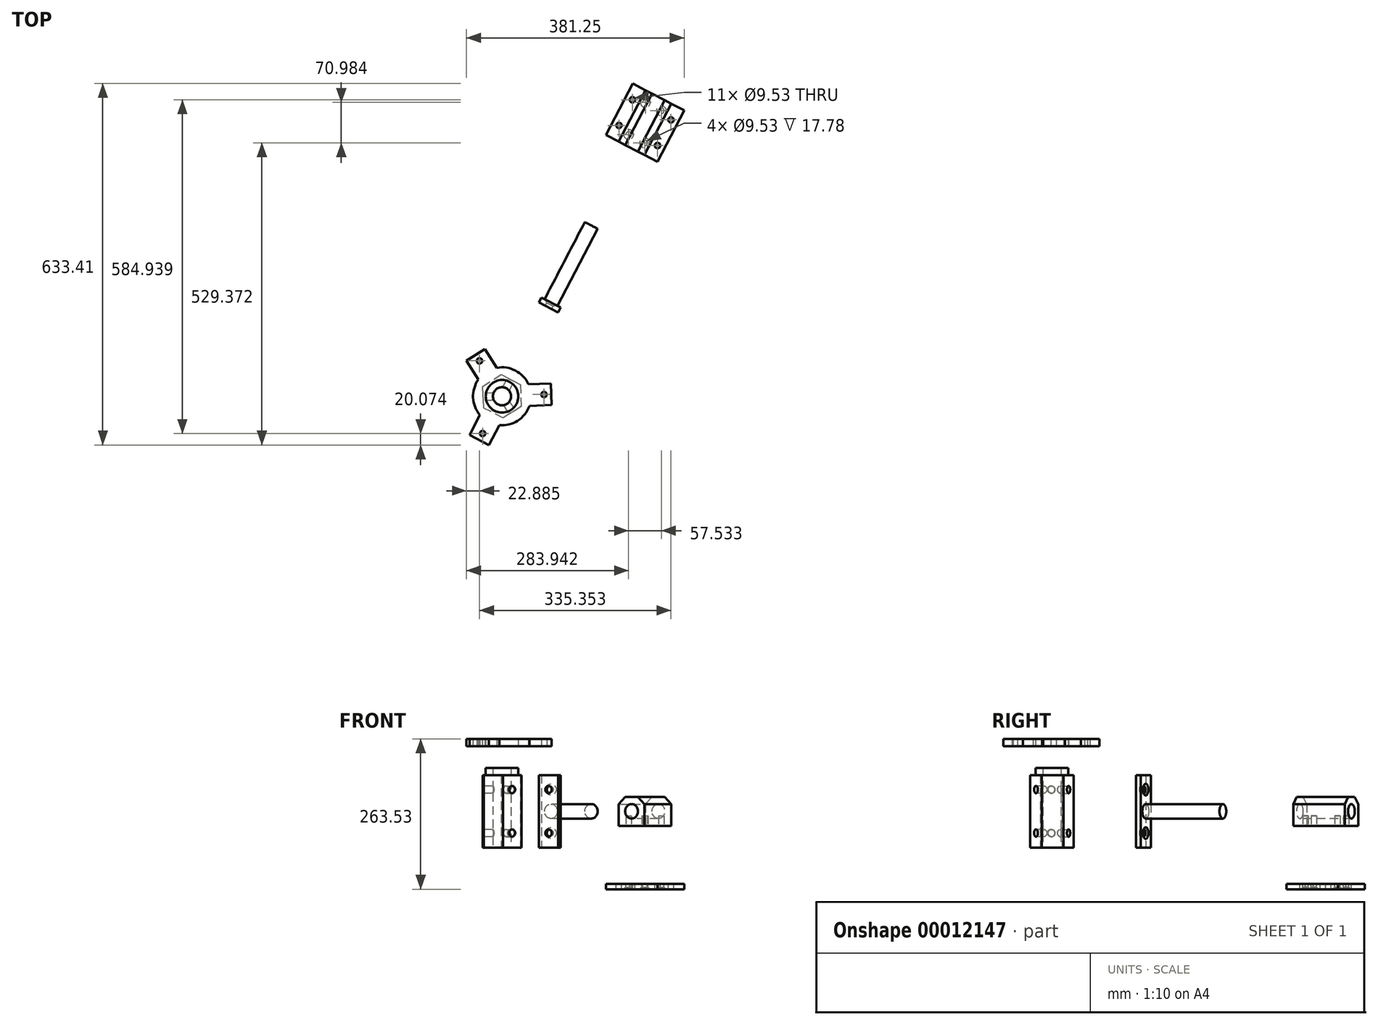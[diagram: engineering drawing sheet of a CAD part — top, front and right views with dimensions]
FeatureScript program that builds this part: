
annotation { "Feature Type Name" : "Feature", "Feature Type Description" : "" }
export const myFeature = defineFeature(function(context is Context, id is Id, definition is map)
    precondition{}
    {
        {
            var Q0;
            Q0=qCreatedBy(makeId("Top.planeOp"),FACE);
            var sketch = newSketch(context, id + "F0", { "sketchPlane" : qUnion([Q0])});
            skCircle(sketch, "E0.cCircle", {"center": v(0, 0) * mm, "radius": 33 * mm, "construction": true});
            skLineSegment(sketch, "E0.0", {"start": v(-1.62, 38.07) * mm, "end": v(32.16, 20.43) * mm});
            skLineSegment(sketch, "E0.1", {"start": v(32.16, 20.43) * mm, "end": v(33.77, -17.63) * mm});
            skLineSegment(sketch, "E0.2", {"start": v(33.77, -17.63) * mm, "end": v(1.62, -38.07) * mm});
            skLineSegment(sketch, "E0.3", {"start": v(1.62, -38.07) * mm, "end": v(-32.16, -20.43) * mm});
            skLineSegment(sketch, "E0.4", {"start": v(-32.16, -20.43) * mm, "end": v(-33.77, 17.63) * mm});
            skLineSegment(sketch, "E0.5", {"start": v(-33.77, 17.63) * mm, "end": v(-1.62, 38.07) * mm});
            skPoint(sketch, "E0.0.midPoint", {"position": v(15.27, 29.25) * mm});
            skCircle(sketch, "E1", {"center": v(0, 0) * mm, "radius": 15.88 * mm});
            skSolve(sketch);
        }
        {
            var Q0;
            Q0=makeQuery(id+"F0.imprint","IMPRINT",FACE,{"disambiguationData":[TD([[makeQuery(id+"F0.imprint","IMPRINT",EDGE,{"derivedFrom":sQuery(id+"F0.wireOp",EDGE,"E0.0")}),-1.0]])]});
            extrude(context, id + "F1", {"entities" : qUnion([Q0]), "depth" : 127 * mm});
        }
        {
            var Q0;
            Q0=makeQuery(id+"F1.opExtrude","SWEPT_FACE",FACE,{"disambiguationData":[OSD([sQuery(id+"F0.wireOp",EDGE,"E0.2")])]});
            var sketch = newSketch(context, id + "F2", { "sketchPlane" : qUnion([Q0]), "disableImprinting" : false});
            skLineSegment(sketch, "E2", {"start": v(0, 127) * mm, "end": v(0, 0) * mm, "construction": true});
            skLineSegment(sketch, "E3", {"start": v(-19.05, 63.5) * mm, "end": v(19.05, 63.5) * mm, "construction": true});
            skLineSegment(sketch, "E4.0", {"start": v(-19.05, 101.6) * mm, "end": v(19.05, 101.6) * mm, "construction": true});
            skLineSegment(sketch, "E5.0", {"start": v(-19.05, 25.4) * mm, "end": v(19.05, 25.4) * mm, "construction": true});
            skCircle(sketch, "E6", {"center": v(0, 101.6) * mm, "radius": 6.35 * mm});
            skCircle(sketch, "E7", {"center": v(0, 25.4) * mm, "radius": 6.35 * mm});
            skSolve(sketch);
        }
        {
            var Q0;
            Q0=makeQuery(id+"F1.opExtrude","SWEPT_FACE",FACE,{"disambiguationData":[OSD([sQuery(id+"F0.wireOp",EDGE,"E0.0")])]});
            var sketch = newSketch(context, id + "F3", { "sketchPlane" : qUnion([Q0]), "disableImprinting" : false});
            skLineSegment(sketch, "E8", {"start": v(0, 127) * mm, "end": v(0, 0) * mm, "construction": true});
            skLineSegment(sketch, "E9", {"start": v(19.05, 63.5) * mm, "end": v(-19.05, 63.5) * mm, "construction": true});
            skLineSegment(sketch, "E10.0", {"start": v(19.05, 101.6) * mm, "end": v(-19.05, 101.6) * mm, "construction": true});
            skLineSegment(sketch, "E11.0", {"start": v(19.05, 25.4) * mm, "end": v(-19.05, 25.4) * mm, "construction": true});
            skCircle(sketch, "E12", {"center": v(0, 101.6) * mm, "radius": 6.35 * mm});
            skCircle(sketch, "E13", {"center": v(0, 25.4) * mm, "radius": 6.35 * mm});
            skSolve(sketch);
        }
        {
            var Q0;
            Q0=makeQuery(id+"F1.opExtrude","SWEPT_FACE",FACE,{"disambiguationData":[OSD([sQuery(id+"F0.wireOp",EDGE,"E0.4")])]});
            var sketch = newSketch(context, id + "F4", { "sketchPlane" : qUnion([Q0])});
            skLineSegment(sketch, "E14", {"start": v(-19.05, 63.5) * mm, "end": v(19.05, 63.5) * mm, "construction": true});
            skLineSegment(sketch, "E15.0", {"start": v(-19.05, 101.6) * mm, "end": v(19.05, 101.6) * mm, "construction": true});
            skLineSegment(sketch, "E16.0", {"start": v(-19.05, 25.4) * mm, "end": v(19.05, 25.4) * mm, "construction": true});
            skLineSegment(sketch, "E17", {"start": v(0, 0) * mm, "end": v(0, 127) * mm, "construction": true});
            skCircle(sketch, "E18", {"center": v(0, 25.4) * mm, "radius": 6.35 * mm});
            skCircle(sketch, "E19", {"center": v(0, 101.6) * mm, "radius": 6.35 * mm});
            skSolve(sketch);
        }
        {
            var Q0;
            Q0=makeQuery(id+"F2.imprint","IMPRINT",FACE,{"disambiguationData":[TD([[makeQuery(id+"F2.imprint","IMPRINT",EDGE,{"derivedFrom":sQuery(id+"F2.wireOp",EDGE,"E6")}),1.0]])]});
            var Q1;
            Q1=makeQuery(id+"F2.imprint","IMPRINT",FACE,{"disambiguationData":[TD([[makeQuery(id+"F2.imprint","IMPRINT",EDGE,{"derivedFrom":sQuery(id+"F2.wireOp",EDGE,"E7")}),1.0]])]});
            var Q2;
            Q2=sQuery(id+"F2.wireOp",EDGE,"E6");
            var Q3;
            Q3=sQuery(id+"F2.wireOp",EDGE,"E7");
            extrude(context, id + "F5", {"entities" : qUnion([Q0, Q1]), "operationType" : NewBodyOperationType.REMOVE, "surfaceEntities" : qUnion([Q2, Q3]), "oppositeDirection" : true, "depth" : 25.4 * mm});
        }
        {
            var Q0;
            Q0=makeQuery(id+"F3.imprint","IMPRINT",FACE,{"disambiguationData":[TD([[makeQuery(id+"F3.imprint","IMPRINT",EDGE,{"derivedFrom":sQuery(id+"F3.wireOp",EDGE,"E12")}),1.0]])]});
            var Q1;
            Q1=makeQuery(id+"F3.imprint","IMPRINT",FACE,{"disambiguationData":[TD([[makeQuery(id+"F3.imprint","IMPRINT",EDGE,{"derivedFrom":sQuery(id+"F3.wireOp",EDGE,"E13")}),1.0]])]});
            extrude(context, id + "F6", {"entities" : qUnion([Q0, Q1]), "operationType" : NewBodyOperationType.REMOVE, "oppositeDirection" : true, "depth" : 25.4 * mm});
        }
        {
            var Q0;
            Q0=makeQuery(id+"F4.imprint","IMPRINT",FACE,{"disambiguationData":[TD([[makeQuery(id+"F4.imprint","IMPRINT",EDGE,{"derivedFrom":sQuery(id+"F4.wireOp",EDGE,"E19")}),1.0]])]});
            var Q1;
            Q1=makeQuery(id+"F4.imprint","IMPRINT",FACE,{"disambiguationData":[TD([[makeQuery(id+"F4.imprint","IMPRINT",EDGE,{"derivedFrom":sQuery(id+"F4.wireOp",EDGE,"E18")}),1.0]])]});
            var Q2;
            Q2=sQuery(id+"F4.wireOp",EDGE,"E19");
            var Q3;
            Q3=sQuery(id+"F4.wireOp",EDGE,"E18");
            extrude(context, id + "F7", {"entities" : qUnion([Q0, Q1]), "operationType" : NewBodyOperationType.REMOVE, "surfaceEntities" : qUnion([Q2, Q3]), "oppositeDirection" : true, "depth" : 25.4 * mm});
        }
        {
            var Q0;
            Q0=makeQuery(id+"F1.opExtrude","CAP_FACE",FACE,{"disambiguationData":[OSD([sQuery(id+"F0.wireOp",EDGE,"E0.0"),sQuery(id+"F0.wireOp",EDGE,"E0.1"),sQuery(id+"F0.wireOp",EDGE,"E0.2"),sQuery(id+"F0.wireOp",EDGE,"E0.3"),sQuery(id+"F0.wireOp",EDGE,"E0.4"),sQuery(id+"F0.wireOp",EDGE,"E0.5"),sQuery(id+"F0.wireOp",EDGE,"E1")])],"isStart":false});
            var sketch = newSketch(context, id + "F8", { "sketchPlane" : qUnion([Q0])});
            skCircle(sketch, "E20", {"center": v(0, 0) * mm, "radius": 28.58 * mm});
            skSolve(sketch);
        }
        {
            var Q0;
            Q0=makeQuery(id+"F8.imprint","IMPRINT",FACE,{"disambiguationData":[TD([[makeQuery(id+"F8.imprint","IMPRINT",EDGE,{"derivedFrom":sQuery(id+"F8.wireOp",EDGE,"E20")}),1.0]])]});
            extrude(context, id + "F9", {"entities" : qUnion([Q0]), "operationType" : NewBodyOperationType.ADD, "depth" : 12.7 * mm});
        }
        {
            var Q0;
            Q0=makeQuery(id+"F1.opExtrude","SWEPT_FACE",FACE,{"disambiguationData":[OSD([sQuery(id+"F0.wireOp",EDGE,"E0.2")])]});
            var sketch = newSketch(context, id + "F10", { "sketchPlane" : qUnion([Q0])});
            skLineSegment(sketch, "E21", {"start": v(-19.05, 0) * mm, "end": v(-187.2, 0) * mm, "construction": true});
            skLineSegment(sketch, "E22", {"start": v(-19.05, 127) * mm, "end": v(-179.85, 127) * mm, "construction": true});
            skLineSegment(sketch, "E23", {"start": v(-95.15, 127) * mm, "end": v(-95.15, 0) * mm});
            skLineSegment(sketch, "E24.0", {"start": v(-133.25, 127) * mm, "end": v(-133.25, 0) * mm});
            skLineSegment(sketch, "E25", {"start": v(-133.25, 127) * mm, "end": v(-95.15, 127) * mm});
            skLineSegment(sketch, "E26", {"start": v(-133.25, 0) * mm, "end": v(-95.15, 0) * mm});
            skPoint(sketch, "E27.orphan", {"position": v(0, 101.6) * mm});
            skPoint(sketch, "E28.orphan", {"position": v(0, 25.4) * mm});
            skCircle(sketch, "E29", {"center": v(-114.2, 101.6) * mm, "radius": 6.35 * mm});
            skCircle(sketch, "E30", {"center": v(-114.2, 25.4) * mm, "radius": 6.35 * mm});
            skLineSegment(sketch, "E31", {"start": v(-133.25, 127) * mm, "end": v(-95.15, 0) * mm, "construction": true});
            skLineSegment(sketch, "E32", {"start": v(-95.15, 127) * mm, "end": v(-133.25, 0) * mm, "construction": true});
            skCircle(sketch, "E33", {"center": v(-114.2, 63.5) * mm, "radius": 12.7 * mm});
            skSolve(sketch);
        }
        {
            var Q0;
            Q0=makeQuery(id+"F10.imprint","IMPRINT",FACE,{"disambiguationData":[TD([[makeQuery(id+"F10.imprint","IMPRINT",EDGE,{"derivedFrom":sQuery(id+"F10.wireOp",EDGE,"E23")}),-1.0]])]});
            extrude(context, id + "F11", {"entities" : qUnion([Q0]), "oppositeDirection" : true, "depth" : 9.52 * mm});
        }
        {
            var Q0;
            Q0=makeQuery(id+"F10.imprint","IMPRINT",FACE,{"disambiguationData":[TD([[makeQuery(id+"F10.imprint","IMPRINT",EDGE,{"derivedFrom":sQuery(id+"F10.wireOp",EDGE,"E33")}),1.0]])]});
            extrude(context, id + "F12", {"entities" : qUnion([Q0]), "operationType" : NewBodyOperationType.ADD, "oppositeDirection" : true, "depth" : 127 * mm});
        }
        {
            var Q0;
            Q0=makeQuery(id+"F11.opExtrude","SWEPT_BODY",BODY,{"disambiguationData":[OSD([sQuery(id+"F10.wireOp",EDGE,"E23"),sQuery(id+"F10.wireOp",EDGE,"E24.0"),sQuery(id+"F10.wireOp",EDGE,"E25"),sQuery(id+"F10.wireOp",EDGE,"E26"),sQuery(id+"F10.wireOp",EDGE,"E29"),sQuery(id+"F10.wireOp",EDGE,"E30"),sQuery(id+"F10.wireOp",EDGE,"E33")])]});
            deleteBodies(context, id + "F13", {"entities" : qUnion([Q0])});
        }
        {
            var Q0;
            Q0=makeQuery(id+"F1.opExtrude","SWEPT_FACE",FACE,{"disambiguationData":[OSD([sQuery(id+"F0.wireOp",EDGE,"E0.0")])]});
            cPlane(context, id + "F14", {"entities" : qUnion([Q0]), "cplaneType" : CPlaneType.OFFSET, "offset" : 152.4 * mm, "width" : 152.4 * mm, "height" : 152.4 * mm});
        }
        {
            var Q0;
            Q0=qCreatedBy(id+"F14.planeOp",FACE);
            var sketch = newSketch(context, id + "F15", { "sketchPlane" : qUnion([Q0])});
            skLineSegment(sketch, "E34.0.0", {"start": v(19.05, 0) * mm, "end": v(-19.05, 0) * mm});
            skLineSegment(sketch, "E34.0.1", {"start": v(19.05, 127) * mm, "end": v(19.05, 0) * mm});
            skLineSegment(sketch, "E34.0.2", {"start": v(19.05, 127) * mm, "end": v(-19.05, 127) * mm});
            skLineSegment(sketch, "E34.0.3", {"start": v(-19.05, 127) * mm, "end": v(-19.05, 0) * mm});
            skCircle(sketch, "E35.0", {"center": v(0, 101.6) * mm, "radius": 6.35 * mm});
            skCircle(sketch, "E35.1", {"center": v(0, 25.4) * mm, "radius": 6.35 * mm});
            skLineSegment(sketch, "E36.0", {"start": v(0, 127) * mm, "end": v(0, 0) * mm, "construction": true});
            skLineSegment(sketch, "E36.1", {"start": v(19.05, 63.5) * mm, "end": v(-19.05, 63.5) * mm, "construction": true});
            skCircle(sketch, "E37", {"center": v(0, 63.5) * mm, "radius": 12.7 * mm});
            skSolve(sketch);
        }
        {
            var Q0;
            Q0=makeQuery(id+"F15.imprint","IMPRINT",FACE,{"disambiguationData":[TD([[makeQuery(id+"F15.imprint","IMPRINT",EDGE,{"derivedFrom":sQuery(id+"F15.wireOp",EDGE,"E37")}),1.0]])]});
            var Q1;
            Q1=sQuery(id+"F15.wireOp",EDGE,"E37");
            extrude(context, id + "F16", {"entities" : qUnion([Q0]), "surfaceEntities" : qUnion([Q1]), "depth" : 152.4 * mm});
        }
        {
            var Q0;
            Q0=makeQuery(id+"F15.imprint","IMPRINT",FACE,{"disambiguationData":[TD([[makeQuery(id+"F15.imprint","IMPRINT",EDGE,{"derivedFrom":sQuery(id+"F15.wireOp",EDGE,"E34.0.0")}),-1.0]])]});
            var Q1;
            Q1=makeQuery(id+"F15.imprint","IMPRINT",FACE,{"disambiguationData":[TD([[makeQuery(id+"F15.imprint","IMPRINT",EDGE,{"derivedFrom":sQuery(id+"F15.wireOp",EDGE,"E37")}),1.0]])]});
            extrude(context, id + "F17", {"entities" : qUnion([Q0, Q1]), "operationType" : NewBodyOperationType.ADD, "oppositeDirection" : true, "depth" : 9.52 * mm});
        }
        {
            var Q0;
            Q0=makeQuery(id+"F17.opExtrude","CAP_EDGE",EDGE,{"disambiguationData":[OSD([sQuery(id+"F15.wireOp",EDGE,"E35.0")])],"isStart":true});
            var Q1;
            Q1=makeQuery(id+"F17.opExtrude","CAP_EDGE",EDGE,{"disambiguationData":[OSD([sQuery(id+"F15.wireOp",EDGE,"E35.1")])],"isStart":true});
            chamfer(context, id + "F18", {"entities" : qUnion([Q0, Q1]), "width" : 3.8 * mm, "tangentPropagation" : true});
        }
        {
            var Q0;
            Q0=qCreatedBy(id+"F14.planeOp",FACE);
            cPlane(context, id + "F19", {"entities" : qUnion([Q0]), "cplaneType" : CPlaneType.OFFSET, "offset" : 304.8 * mm, "width" : 152.4 * mm, "height" : 152.4 * mm});
        }
        {
            var Q0;
            Q0=qCreatedBy(id+"F19.planeOp",FACE);
            var sketch = newSketch(context, id + "F20", { "sketchPlane" : qUnion([Q0])});
            skCircle(sketch, "E38.0", {"center": v(0, 63.5) * mm, "radius": 12.7 * mm});
            skCircle(sketch, "E39.cCircle", {"center": v(0, 63.5) * mm, "radius": 25.4 * mm, "construction": true});
            skLineSegment(sketch, "E39.0", {"start": v(25.4, 88.9) * mm, "end": v(25.4, 38.1) * mm});
            skLineSegment(sketch, "E39.1", {"start": v(25.4, 38.1) * mm, "end": v(-25.4, 38.1) * mm});
            skLineSegment(sketch, "E39.2", {"start": v(-25.4, 38.1) * mm, "end": v(-25.4, 88.9) * mm});
            skLineSegment(sketch, "E39.3", {"start": v(-25.4, 88.9) * mm, "end": v(25.4, 88.9) * mm});
            skPoint(sketch, "E39.0.midPoint", {"position": v(25.4, 63.5) * mm});
            skSolve(sketch);
        }
        {
            var Q0;
            Q0=makeQuery(id+"F20.imprint","IMPRINT",FACE,{"disambiguationData":[TD([[makeQuery(id+"F20.imprint","IMPRINT",EDGE,{"derivedFrom":sQuery(id+"F20.wireOp",EDGE,"E38.0")}),-1.0]])]});
            extrude(context, id + "F21", {"entities" : qUnion([Q0]), "depth" : 101.6 * mm});
        }
        {
            var Q0;
            Q0=makeQuery(id+"F21.opExtrude","SWEPT_EDGE",EDGE,{"disambiguationData":[OSD([sQuery(id+"F20.wireOp",EDGE,"E39.2"),sQuery(id+"F20.wireOp",EDGE,"E39.3")])]});
            var Q1;
            Q1=makeQuery(id+"F21.opExtrude","SWEPT_EDGE",EDGE,{"disambiguationData":[OSD([sQuery(id+"F20.wireOp",EDGE,"E39.0"),sQuery(id+"F20.wireOp",EDGE,"E39.3")])]});
            chamfer(context, id + "F22", {"entities" : qUnion([Q0, Q1]), "width" : 12.7 * mm, "tangentPropagation" : true});
        }
        {
            var Q0;
            Q0=makeQuery(id+"F21.opExtrude","SWEPT_FACE",FACE,{"disambiguationData":[OSD([sQuery(id+"F20.wireOp",EDGE,"E39.1")])]});
            var sketch = newSketch(context, id + "F23", { "sketchPlane" : qUnion([Q0])});
            skLineSegment(sketch, "E40", {"start": v(226.86, -434.54) * mm, "end": v(273.88, -524.6) * mm, "construction": true});
            skLineSegment(sketch, "E41", {"start": v(272.88, -467.82) * mm, "end": v(227.85, -491.33) * mm, "construction": true});
            skLineSegment(sketch, "E42.0", {"start": v(210.34, -464.65) * mm, "end": v(255.38, -441.14) * mm, "construction": true});
            skLineSegment(sketch, "E43.0", {"start": v(239.73, -520.94) * mm, "end": v(284.76, -497.43) * mm, "construction": true});
            skLineSegment(sketch, "E44.0", {"start": v(287.95, -517.26) * mm, "end": v(240.93, -427.2) * mm, "construction": true});
            skLineSegment(sketch, "E45.0", {"start": v(259.8, -531.95) * mm, "end": v(212.79, -441.89) * mm, "construction": true});
            skCircle(sketch, "E46", {"center": v(279.13, -500.37) * mm, "radius": 4.76 * mm});
            skCircle(sketch, "E47", {"center": v(250.99, -515.07) * mm, "radius": 4.76 * mm});
            skCircle(sketch, "E48", {"center": v(221.6, -458.78) * mm, "radius": 4.76 * mm});
            skCircle(sketch, "E49", {"center": v(249.75, -444.08) * mm, "radius": 4.76 * mm});
            skSolve(sketch);
        }
        {
            var Q0;
            Q0=makeQuery(id+"F21.opExtrude","SWEPT_FACE",FACE,{"disambiguationData":[OSD([sQuery(id+"F20.wireOp",EDGE,"E39.1")])]});
            cPlane(context, id + "F24", {"entities" : qUnion([Q0]), "cplaneType" : CPlaneType.OFFSET, "offset" : 101.6 * mm, "width" : 152.4 * mm, "height" : 152.4 * mm});
        }
        {
            var Q0;
            Q0=makeQuery(id+"F23.imprint","IMPRINT",FACE,{"disambiguationData":[TD([[makeQuery(id+"F23.imprint","IMPRINT",EDGE,{"derivedFrom":sQuery(id+"F23.wireOp",EDGE,"E46")}),1.0]])]});
            var Q1;
            Q1=makeQuery(id+"F23.imprint","IMPRINT",FACE,{"disambiguationData":[TD([[makeQuery(id+"F23.imprint","IMPRINT",EDGE,{"derivedFrom":sQuery(id+"F23.wireOp",EDGE,"E47")}),1.0]])]});
            var Q2;
            Q2=makeQuery(id+"F23.imprint","IMPRINT",FACE,{"disambiguationData":[TD([[makeQuery(id+"F23.imprint","IMPRINT",EDGE,{"derivedFrom":sQuery(id+"F23.wireOp",EDGE,"E49")}),1.0]])]});
            var Q3;
            Q3=makeQuery(id+"F23.imprint","IMPRINT",FACE,{"disambiguationData":[TD([[makeQuery(id+"F23.imprint","IMPRINT",EDGE,{"derivedFrom":sQuery(id+"F23.wireOp",EDGE,"E48")}),1.0]])]});
            var Q4;
            Q4=sQuery(id+"F23.wireOp",EDGE,"E46");
            var Q5;
            Q5=sQuery(id+"F23.wireOp",EDGE,"E47");
            var Q6;
            Q6=sQuery(id+"F23.wireOp",EDGE,"E48");
            var Q7;
            Q7=sQuery(id+"F23.wireOp",EDGE,"E49");
            extrude(context, id + "F25", {"entities" : qUnion([Q0, Q1, Q2, Q3]), "operationType" : NewBodyOperationType.REMOVE, "surfaceEntities" : qUnion([Q4, Q5, Q6, Q7]), "oppositeDirection" : true, "depth" : 17.78 * mm});
        }
        {
            var Q0;
            Q0=qCreatedBy(id+"F24.planeOp",FACE);
            var sketch = newSketch(context, id + "F26", { "sketchPlane" : qUnion([Q0])});
            skLineSegment(sketch, "E50.0.0", {"start": v(204.34, -446.3) * mm, "end": v(249.38, -422.79) * mm, "construction": true});
            skLineSegment(sketch, "E50.0.1", {"start": v(251.36, -536.36) * mm, "end": v(204.34, -446.3) * mm, "construction": true});
            skLineSegment(sketch, "E50.0.2", {"start": v(251.36, -536.36) * mm, "end": v(296.4, -512.85) * mm, "construction": true});
            skLineSegment(sketch, "E50.0.3", {"start": v(296.4, -512.85) * mm, "end": v(249.38, -422.79) * mm, "construction": true});
            skLineSegment(sketch, "E51.0", {"start": v(228.85, -548.12) * mm, "end": v(181.83, -458.05) * mm});
            skLineSegment(sketch, "E52.0", {"start": v(318.91, -501.1) * mm, "end": v(271.9, -411.03) * mm});
            skLineSegment(sketch, "E53", {"start": v(318.91, -501.1) * mm, "end": v(228.85, -548.12) * mm});
            skLineSegment(sketch, "E54", {"start": v(181.83, -458.05) * mm, "end": v(271.9, -411.03) * mm});
            skLineSegment(sketch, "E55.0", {"start": v(193.58, -480.57) * mm, "end": v(283.65, -433.55) * mm, "construction": true});
            skLineSegment(sketch, "E56.0", {"start": v(307.16, -478.58) * mm, "end": v(217.1, -525.6) * mm, "construction": true});
            skLineSegment(sketch, "E57.0", {"start": v(240.1, -542.24) * mm, "end": v(193.08, -452.17) * mm, "construction": true});
            skLineSegment(sketch, "E58.0", {"start": v(307.65, -506.97) * mm, "end": v(260.63, -416.9) * mm, "construction": true});
            skCircle(sketch, "E59", {"center": v(228.35, -519.72) * mm, "radius": 4.76 * mm});
            skCircle(sketch, "E60", {"center": v(295.9, -484.46) * mm, "radius": 4.76 * mm});
            skCircle(sketch, "E61", {"center": v(272.39, -439.43) * mm, "radius": 4.76 * mm});
            skCircle(sketch, "E62", {"center": v(204.84, -474.7) * mm, "radius": 4.76 * mm});
            skCircle(sketch, "E63.0", {"center": v(250.99, -515.07) * mm, "radius": 4.76 * mm});
            skCircle(sketch, "E63.1", {"center": v(221.6, -458.78) * mm, "radius": 4.76 * mm});
            skCircle(sketch, "E63.2", {"center": v(249.75, -444.08) * mm, "radius": 4.76 * mm});
            skCircle(sketch, "E63.3", {"center": v(279.13, -500.37) * mm, "radius": 4.76 * mm});
            skSolve(sketch);
        }
        {
            var Q0;
            Q0=makeQuery(id+"F26.imprint","IMPRINT",FACE,{"disambiguationData":[TD([[makeQuery(id+"F26.imprint","IMPRINT",EDGE,{"derivedFrom":sQuery(id+"F26.wireOp",EDGE,"E51.0")}),-1.0]])]});
            extrude(context, id + "F27", {"entities" : qUnion([Q0]), "depth" : 9.52 * mm});
        }
        {
            var Q0;
            Q0=makeQuery(id+"F27.opExtrude","CAP_EDGE",EDGE,{"disambiguationData":[OSD([sQuery(id+"F26.wireOp",EDGE,"E63.1")])],"isStart":false});
            var Q1;
            Q1=makeQuery(id+"F27.opExtrude","CAP_EDGE",EDGE,{"disambiguationData":[OSD([sQuery(id+"F26.wireOp",EDGE,"E63.2")])],"isStart":false});
            var Q2;
            Q2=makeQuery(id+"F27.opExtrude","CAP_EDGE",EDGE,{"disambiguationData":[OSD([sQuery(id+"F26.wireOp",EDGE,"E63.3")])],"isStart":false});
            var Q3;
            Q3=makeQuery(id+"F27.opExtrude","CAP_EDGE",EDGE,{"disambiguationData":[OSD([sQuery(id+"F26.wireOp",EDGE,"E63.0")])],"isStart":false});
            chamfer(context, id + "F28", {"entities" : qUnion([Q0, Q1, Q2, Q3]), "width" : 3.8 * mm, "tangentPropagation" : true});
        }
        {
            var Q0;
            Q0=makeQuery(id+"F1.opExtrude","CAP_FACE",FACE,{"disambiguationData":[OSD([sQuery(id+"F0.wireOp",EDGE,"E0.0"),sQuery(id+"F0.wireOp",EDGE,"E0.1"),sQuery(id+"F0.wireOp",EDGE,"E0.2"),sQuery(id+"F0.wireOp",EDGE,"E0.3"),sQuery(id+"F0.wireOp",EDGE,"E0.4"),sQuery(id+"F0.wireOp",EDGE,"E0.5"),sQuery(id+"F0.wireOp",EDGE,"E1")])],"isStart":false});
            cPlane(context, id + "F29", {"entities" : qUnion([Q0]), "cplaneType" : CPlaneType.OFFSET, "offset" : 50.8 * mm, "width" : 152.4 * mm, "height" : 152.4 * mm});
        }
        {
            var Q0;
            Q0=qCreatedBy(id+"F29.planeOp",FACE);
            var sketch = newSketch(context, id + "F30", { "sketchPlane" : qUnion([Q0])});
            skPoint(sketch, "E64.0", {"position": v(0, 0) * mm});
            skArc(sketch, "E65", {"start": v(46.24, 21.03) * mm, "mid": v(23.5, 45.03) * mm, "end": v(-9.18, 49.96) * mm});
            skLineSegment(sketch, "E66", {"start": v(46.24, 21.03) * mm, "end": v(85.38, 22.7) * mm});
            skLineSegment(sketch, "E67", {"start": v(47.86, -17.03) * mm, "end": v(87, -15.37) * mm});
            skLineSegment(sketch, "E68", {"start": v(85.38, 22.7) * mm, "end": v(87, -15.37) * mm});
            skPoint(sketch, "E69.orphan", {"position": v(121.8, 24.24) * mm});
            skLineSegment(sketch, "E70.1.0", {"start": v(-9.18, 49.96) * mm, "end": v(-30.19, 83.03) * mm});
            skLineSegment(sketch, "E70.1.1", {"start": v(-62.34, 62.6) * mm, "end": v(-30.19, 83.03) * mm});
            skLineSegment(sketch, "E70.1.2", {"start": v(-41.33, 29.53) * mm, "end": v(-62.34, 62.6) * mm});
            skLineSegment(sketch, "E70.2.0", {"start": v(-38.68, -32.93) * mm, "end": v(-56.81, -67.66) * mm});
            skLineSegment(sketch, "E70.2.1", {"start": v(-23.04, -85.29) * mm, "end": v(-56.81, -67.66) * mm});
            skLineSegment(sketch, "E70.2.2", {"start": v(-4.9, -50.56) * mm, "end": v(-23.04, -85.29) * mm});
            skArc(sketch, "E71.trimOffspring", {"start": v(-4.9, -50.56) * mm, "mid": v(27.24, -42.88) * mm, "end": v(47.86, -17.03) * mm});
            skArc(sketch, "E72.trimOffspring", {"start": v(-41.33, 29.53) * mm, "mid": v(-50.75, -2.16) * mm, "end": v(-38.68, -32.93) * mm});
            skCircle(sketch, "E73.0", {"center": v(0, 0) * mm, "radius": 28.58 * mm});
            skLineSegment(sketch, "E74", {"start": v(86.2, 3.66) * mm, "end": v(0, 0) * mm, "construction": true});
            skLineSegment(sketch, "E75.0", {"start": v(72.7, 22.16) * mm, "end": v(74.31, -15.91) * mm, "construction": true});
            skCircle(sketch, "E76", {"center": v(73.5, 3.12) * mm, "radius": 4.76 * mm});
            skCircle(sketch, "E77.1.0", {"center": v(-39.46, 62.1) * mm, "radius": 4.76 * mm});
            skCircle(sketch, "E77.2.0", {"center": v(-34.05, -65.22) * mm, "radius": 4.76 * mm});
            skSolve(sketch);
        }
        {
            var Q0;
            Q0=makeQuery(id+"F30.imprint","IMPRINT",FACE,{"disambiguationData":[TD([[makeQuery(id+"F30.imprint","IMPRINT",EDGE,{"derivedFrom":sQuery(id+"F30.wireOp",EDGE,"E65")}),1.0]])]});
            extrude(context, id + "F31", {"entities" : qUnion([Q0]), "depth" : 12.7 * mm});
        }
    });
